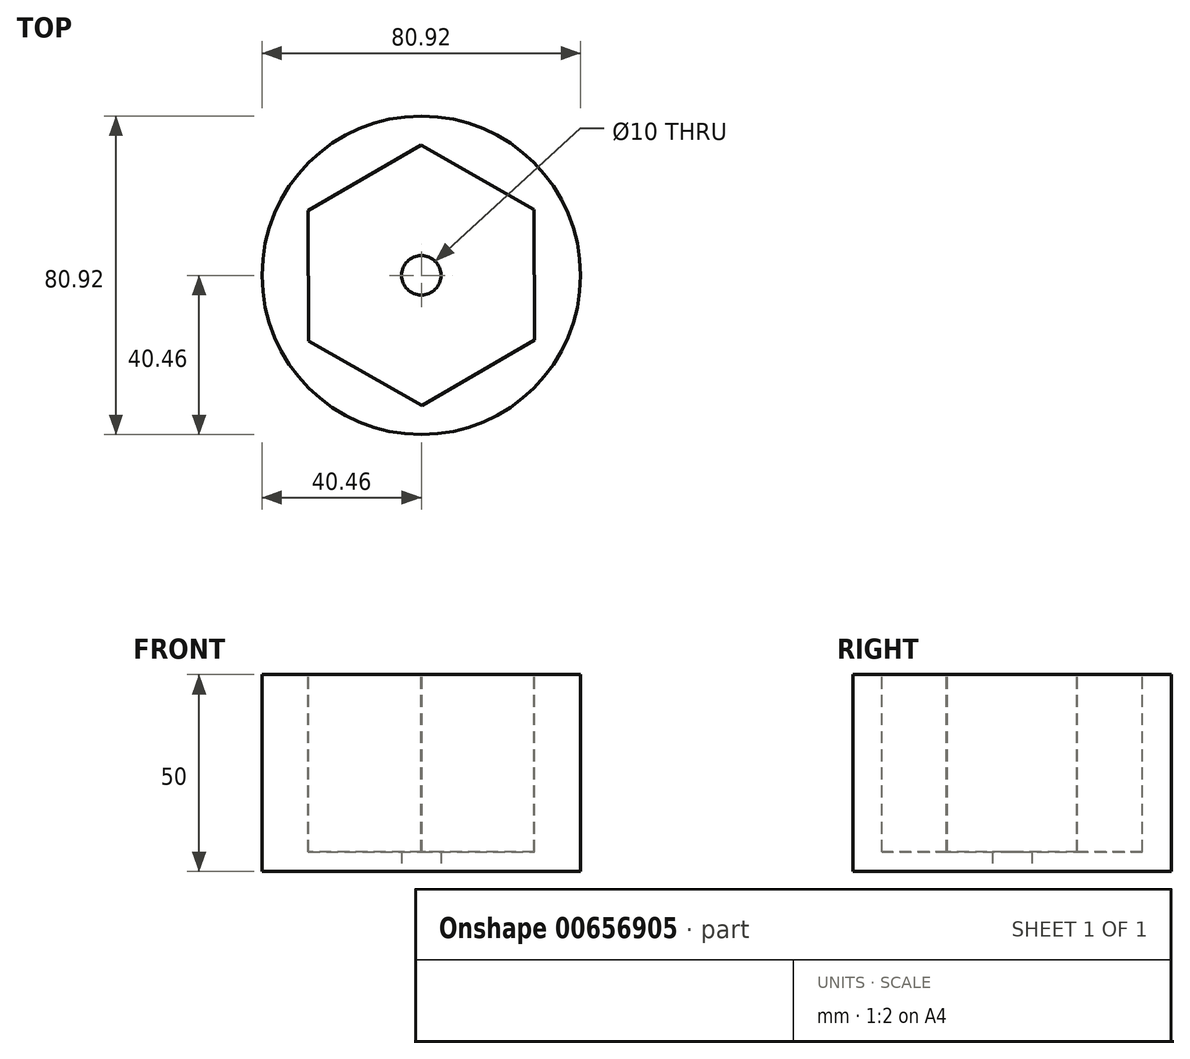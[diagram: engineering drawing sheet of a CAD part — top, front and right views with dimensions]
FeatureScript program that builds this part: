
annotation { "Feature Type Name" : "Feature", "Feature Type Description" : "" }
export const myFeature = defineFeature(function(context is Context, id is Id, definition is map)
    precondition{}
    {
        {
            var Q0;
            Q0=qCreatedBy(makeId("Top.planeOp"),FACE);
            var sketch = newSketch(context, id + "F0", { "sketchPlane" : qUnion([Q0])});
            skCircle(sketch, "E0", {"center": v(0, 0) * mm, "radius": 40.46 * mm});
            skSolve(sketch);
        }
        {
            var Q0;
            Q0 = qSketchRegion(id + "F0", true);
            extrude(context, id + "F1", {"entities" : qUnion([Q0]), "depth" : 50 * mm, "offsetDistance" : 25 * mm});
        }
        {
            var Q0;
            Q0=makeQuery(id+"F1.opExtrude","CAP_FACE",FACE,{"disambiguationData":[OSD([sQuery(id+"F0.wireOp",EDGE,"E0")])],"isStart":false});
            var sketch = newSketch(context, id + "F2", { "sketchPlane" : qUnion([Q0])});
            skCircle(sketch, "E1.cCircle", {"center": v(0, 0) * mm, "radius": 28.66 * mm, "construction": true});
            skLineSegment(sketch, "E1.0", {"start": v(-28.73, 16.44) * mm, "end": v(-0.13, 33.1) * mm});
            skLineSegment(sketch, "E1.1", {"start": v(-0.13, 33.1) * mm, "end": v(28.6, 16.66) * mm});
            skLineSegment(sketch, "E1.2", {"start": v(28.6, 16.66) * mm, "end": v(28.73, -16.44) * mm});
            skLineSegment(sketch, "E1.3", {"start": v(28.73, -16.44) * mm, "end": v(0.13, -33.1) * mm});
            skLineSegment(sketch, "E1.4", {"start": v(0.13, -33.1) * mm, "end": v(-28.6, -16.66) * mm});
            skLineSegment(sketch, "E1.5", {"start": v(-28.6, -16.66) * mm, "end": v(-28.73, 16.44) * mm});
            skPoint(sketch, "E1.0.midPoint", {"position": v(-14.43, 24.77) * mm});
            skSolve(sketch);
        }
        {
            var Q0;
            Q0=makeQuery(id+"F2.imprint","IMPRINT",FACE,{"disambiguationData":[TD([[makeQuery(id+"F2.imprint","IMPRINT",EDGE,{"derivedFrom":sQuery(id+"F2.wireOp",EDGE,"E1.0")}),-1.0]])]});
            extrude(context, id + "F3", {"entities" : qUnion([Q0]), "operationType" : NewBodyOperationType.REMOVE, "oppositeDirection" : true, "depth" : 45 * mm, "offsetDistance" : 25 * mm});
        }
        {
            var Q0;
            Q0=qCreatedBy(makeId("Front.planeOp"),FACE);
            cPlane(context, id + "F4", {"entities" : qUnion([Q0]), "cplaneType" : CPlaneType.OFFSET, "offset" : 50 * mm, "width" : 150 * mm, "height" : 150 * mm});
        }
        {
            var Q0;
            Q0=sQuery(id+"F0.wireOp",VERTEX,"E0.center");
            var Q1;
            Q1=makeQuery(id+"F1.opExtrude","SWEPT_BODY",BODY,{"disambiguationData":[OSD([sQuery(id+"F0.wireOp",EDGE,"E0")])]});
            hole(context, id + "F5", {"style" : HoleStyle.SIMPLE, "endStyle" : HoleEndStyle.THROUGH, "oppositeDirection" : true, "holeDiameter" : 10 * mm, "majorDiameter" : 5 * mm, "isTappedThrough" : true, "tappedDepth" : 12 * mm, "tapClearance" : 3, "locations" : qUnion([Q0]), "scope" : qUnion([Q1])});
        }
    });
